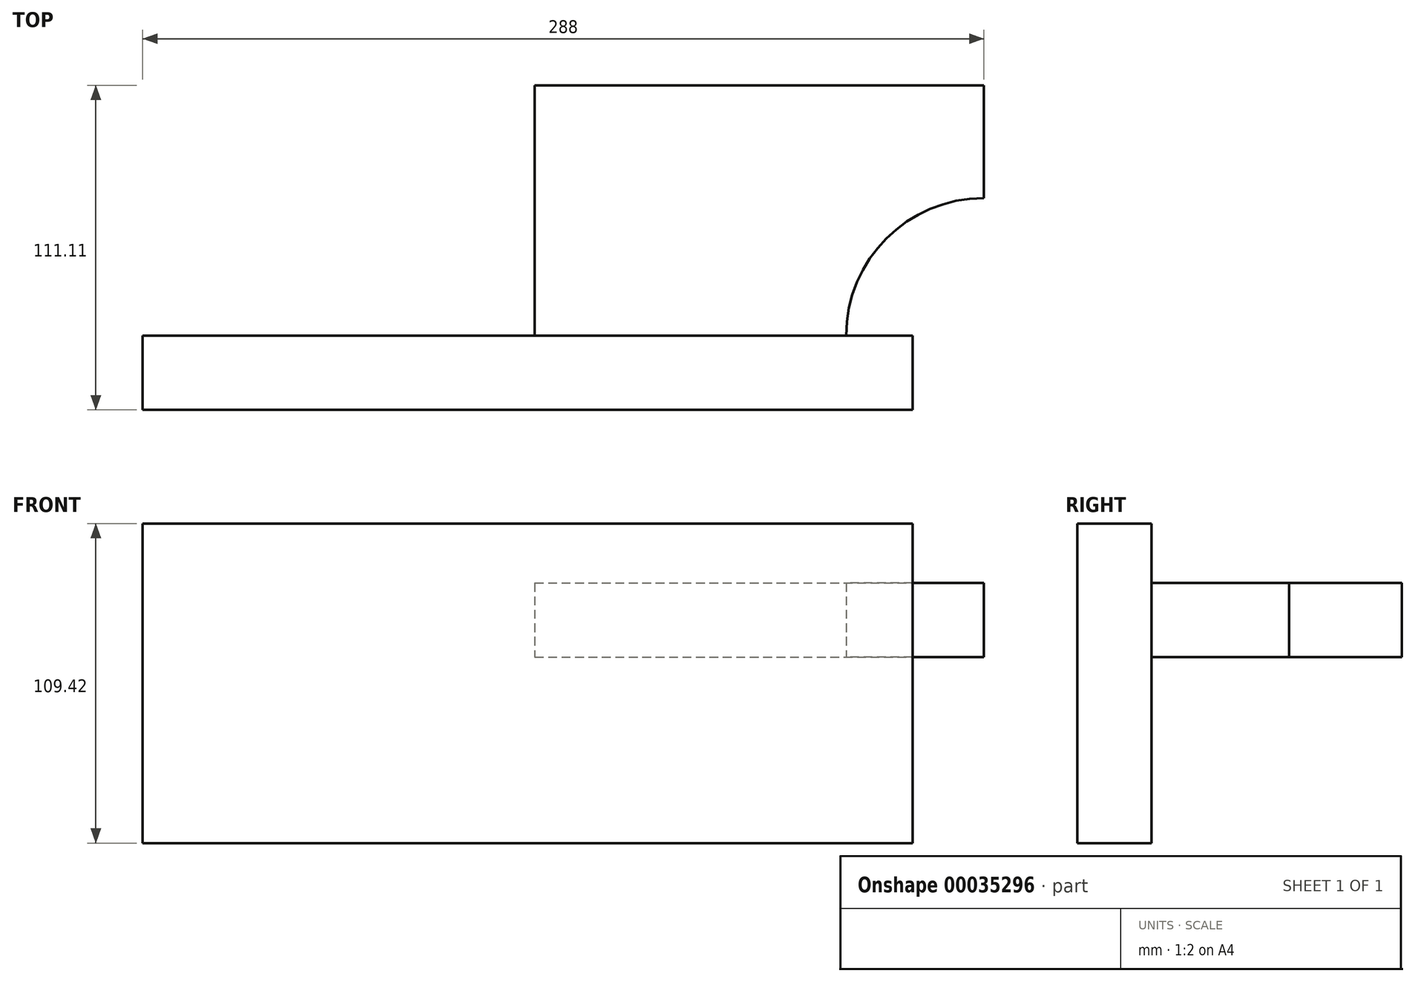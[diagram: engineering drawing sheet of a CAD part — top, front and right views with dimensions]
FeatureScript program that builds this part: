
annotation { "Feature Type Name" : "Feature", "Feature Type Description" : "" }
export const myFeature = defineFeature(function(context is Context, id is Id, definition is map)
    precondition{}
    {
        {
            var Q0;
            Q0=qCreatedBy(makeId("Front.planeOp"),FACE);
            var sketch = newSketch(context, id + "F0", { "sketchPlane" : qUnion([Q0])});
            skLineSegment(sketch, "E0.bottom", {"start": v(-116.56, 35) * mm, "end": v(110.46, 35) * mm});
            skLineSegment(sketch, "E0.top", {"start": v(-116.56, -45.92) * mm, "end": v(110.46, -45.92) * mm});
            skLineSegment(sketch, "E0.left", {"start": v(-116.56, 35) * mm, "end": v(-116.56, -45.92) * mm});
            skLineSegment(sketch, "E0.right", {"start": v(110.46, 35) * mm, "end": v(110.46, -45.92) * mm});
            skLineSegment(sketch, "E1.bottom", {"start": v(-134.26, 45.77) * mm, "end": v(129.38, 45.77) * mm});
            skLineSegment(sketch, "E1.top", {"start": v(-134.26, -63.65) * mm, "end": v(129.38, -63.65) * mm});
            skLineSegment(sketch, "E1.left", {"start": v(-134.26, 45.77) * mm, "end": v(-134.26, -63.65) * mm});
            skLineSegment(sketch, "E1.right", {"start": v(129.38, 45.77) * mm, "end": v(129.38, -63.65) * mm});
            skSolve(sketch);
        }
        {
            var Q0;
            Q0=makeQuery(id+"F0.imprint","IMPRINT",FACE,{"disambiguationData":[TD([[makeQuery(id+"F0.imprint","IMPRINT",EDGE,{"derivedFrom":sQuery(id+"F0.wireOp",EDGE,"E0.bottom")}),-1.0]])]});
            var Q1;
            Q1=makeQuery(id+"F0.imprint","IMPRINT",FACE,{"disambiguationData":[TD([[makeQuery(id+"F0.imprint","IMPRINT",EDGE,{"derivedFrom":sQuery(id+"F0.wireOp",EDGE,"E0.bottom")}),1.0]])]});
            extrude(context, id + "F1", {"entities" : qUnion([Q0, Q1]), "depth" : 25.4 * mm});
        }
        {
            var Q0;
            Q0=qCreatedBy(makeId("Top.planeOp"),FACE);
            var sketch = newSketch(context, id + "F2", { "sketchPlane" : qUnion([Q0])});
            skLineSegment(sketch, "E2.bottom", {"start": v(0, 0) * mm, "end": v(153.74, 0) * mm});
            skLineSegment(sketch, "E2.top", {"start": v(0, 85.71) * mm, "end": v(153.74, 85.71) * mm});
            skLineSegment(sketch, "E2.left", {"start": v(0, 0) * mm, "end": v(0, 85.71) * mm});
            skLineSegment(sketch, "E2.right", {"start": v(153.74, 0) * mm, "end": v(153.74, 85.71) * mm});
            skCircle(sketch, "E3", {"center": v(153.74, 0) * mm, "radius": 47.13 * mm});
            skSolve(sketch);
        }
        {
            var Q0;
            {var subQ5=sQuery(id+"F2.wireOp",EDGE,"E2.top");Q0=makeQuery(id+"F2.imprint","IMPRINT",FACE,{"disambiguationData":[TD([[makeQuery(id+"F2.imprint","IMPRINT",EDGE,{"derivedFrom":subQ5}),-1.0]])]});}
            var Q1;
            Q1=makeQuery(id+"F1.opExtrude","SWEPT_BODY",BODY,{"disambiguationData":[OSD([sQuery(id+"F0.wireOp",EDGE,"E1.bottom"),sQuery(id+"F0.wireOp",EDGE,"E1.top"),sQuery(id+"F0.wireOp",EDGE,"E1.left"),sQuery(id+"F0.wireOp",EDGE,"E1.right")])]});
            extrude(context, id + "F3", {"entities" : qUnion([Q0]), "operationType" : NewBodyOperationType.ADD, "endBoundEntityBody" : qUnion([Q1]), "depth" : 25.4 * mm});
        }
    });
